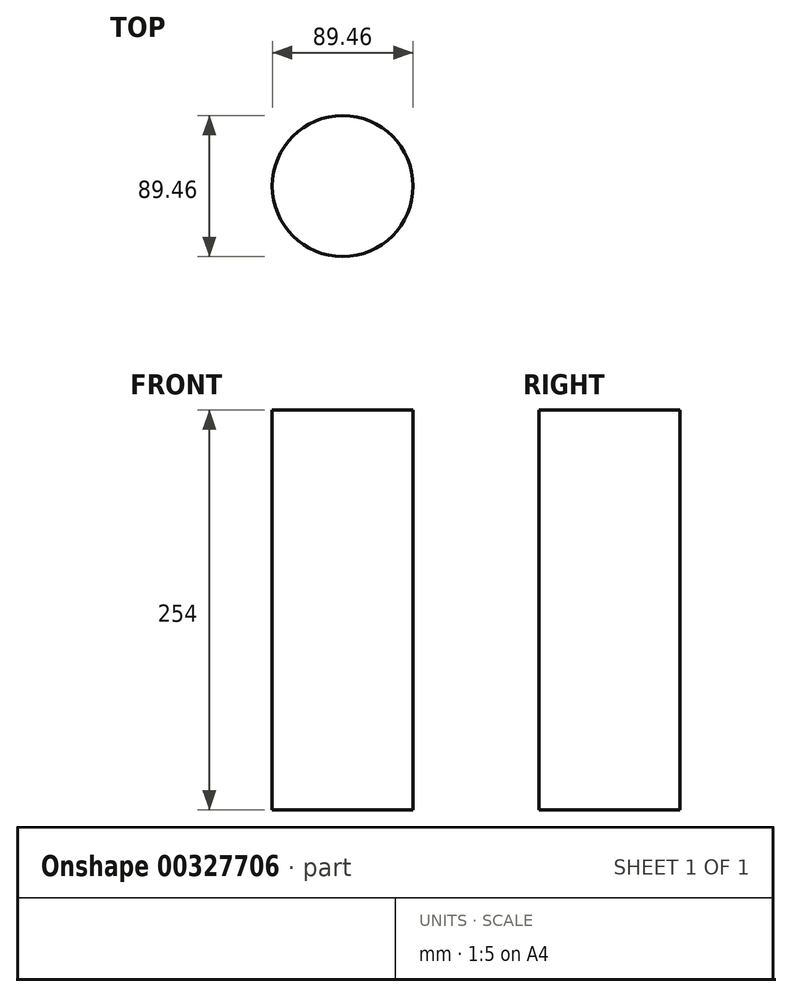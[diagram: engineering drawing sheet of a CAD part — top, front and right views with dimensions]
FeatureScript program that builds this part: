
annotation { "Feature Type Name" : "Feature", "Feature Type Description" : "" }
export const myFeature = defineFeature(function(context is Context, id is Id, definition is map)
    precondition{}
    {
        {
            var Q0;
            Q0=qCreatedBy(makeId("Top.planeOp"),FACE);
            var sketch = newSketch(context, id + "F0", { "sketchPlane" : qUnion([Q0])});
            skCircle(sketch, "E0", {"center": v(0, 0) * mm, "radius": 44.73 * mm});
            skSolve(sketch);
        }
        {
            var Q0;
            Q0=sQuery(id+"F0.wireOp",EDGE,"E0");
            extrude(context, id + "F1", {"bodyType" : ToolBodyType.SURFACE, "surfaceEntities" : qUnion([Q0]), "depth" : 254 * mm});
        }
    });
